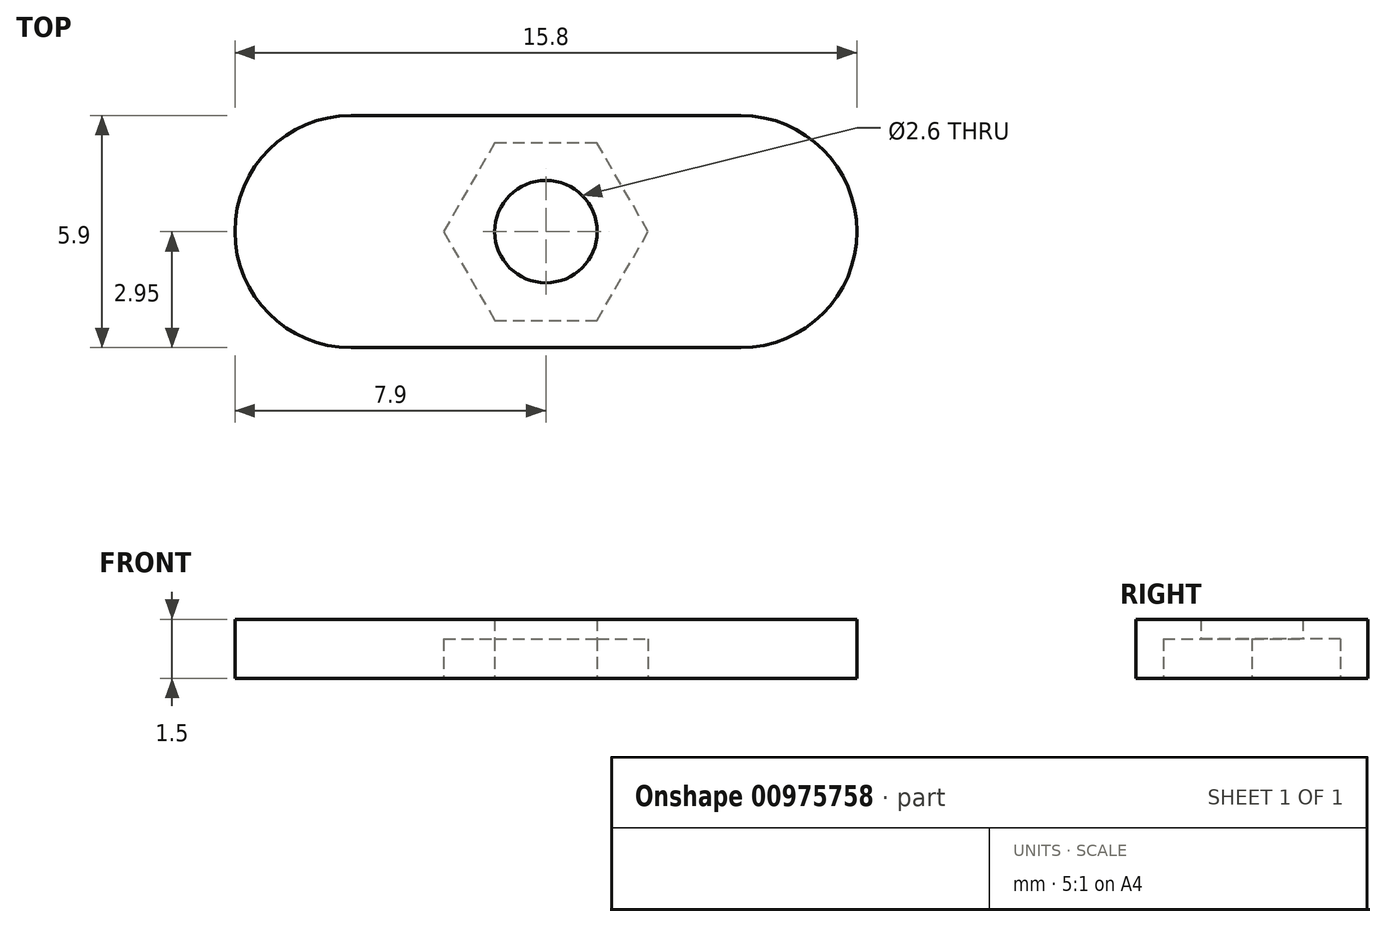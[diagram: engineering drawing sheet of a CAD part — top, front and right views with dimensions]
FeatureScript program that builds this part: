
annotation { "Feature Type Name" : "Feature", "Feature Type Description" : "" }
export const myFeature = defineFeature(function(context is Context, id is Id, definition is map)
    precondition{}
    {
        {
            var Q0;
            Q0=qCreatedBy(makeId("Top.planeOp"),FACE);
            var sketch = newSketch(context, id + "F0", { "sketchPlane" : qUnion([Q0])});
            skLineSegment(sketch, "E0", {"start": v(0, 0) * mm, "end": v(4.95, 0) * mm});
            skLineSegment(sketch, "E1", {"start": v(0, 0) * mm, "end": v(-4.95, 0) * mm});
            skCircle(sketch, "E2", {"center": v(-4.95, 0) * mm, "radius": 2.95 * mm});
            skCircle(sketch, "E3", {"center": v(4.95, 0) * mm, "radius": 2.95 * mm});
            skLineSegment(sketch, "E4", {"start": v(4.95, 0) * mm, "end": v(4.95, 2.95) * mm});
            skLineSegment(sketch, "E5", {"start": v(4.95, 2.95) * mm, "end": v(-4.95, 2.95) * mm});
            skLineSegment(sketch, "E6", {"start": v(-4.95, -2.95) * mm, "end": v(4.95, -2.95) * mm});
            skSolve(sketch);
        }
        {
            var Q0;
            Q0 = qSketchRegion(id + "F0", true);
            extrude(context, id + "F1", {"entities" : qUnion([Q0]), "depth" : 1.5 * mm, "offsetDistance" : 25 * mm});
        }
        {
            var Q0;
            Q0=makeQuery(id+"F1.opExtrude","CAP_FACE",FACE,{"disambiguationData":[OSD([sQuery(id+"F0.wireOp",EDGE,"E2"),sQuery(id+"F0.wireOp",EDGE,"E3"),sQuery(id+"F0.wireOp",EDGE,"E5"),sQuery(id+"F0.wireOp",EDGE,"E6")])],"isStart":true});
            var sketch = newSketch(context, id + "F2", { "sketchPlane" : qUnion([Q0])});
            skCircle(sketch, "E7", {"center": v(0, 0) * mm, "radius": 2.6 * mm});
            skCircle(sketch, "E8.cCircle", {"center": v(0, 0) * mm, "radius": 2.6 * mm, "construction": true});
            skLineSegment(sketch, "E8.0", {"start": v(-2.6, 0) * mm, "end": v(-1.3, 2.25) * mm});
            skLineSegment(sketch, "E8.1", {"start": v(-1.3, 2.25) * mm, "end": v(1.3, 2.25) * mm});
            skLineSegment(sketch, "E8.2", {"start": v(1.3, 2.25) * mm, "end": v(2.6, 0) * mm});
            skLineSegment(sketch, "E8.3", {"start": v(2.6, 0) * mm, "end": v(1.3, -2.25) * mm});
            skLineSegment(sketch, "E8.4", {"start": v(1.3, -2.25) * mm, "end": v(-1.3, -2.25) * mm});
            skLineSegment(sketch, "E8.5", {"start": v(-1.3, -2.25) * mm, "end": v(-2.6, 0) * mm});
            skSolve(sketch);
        }
        {
            var Q0;
            Q0=makeQuery(id+"F2.imprint","IMPRINT",FACE,{"disambiguationData":[TD([[makeQuery(id+"F2.imprint","IMPRINT",EDGE,{"derivedFrom":sQuery(id+"F2.wireOp",EDGE,"E8.0")}),-1.0]])]});
            extrude(context, id + "F3", {"entities" : qUnion([Q0]), "operationType" : NewBodyOperationType.REMOVE, "oppositeDirection" : true, "depth" : 1 * mm, "offsetDistance" : 25 * mm});
        }
        {
            var Q0;
            Q0=makeQuery(id+"F3.boolean.opBoolean","COPY",FACE,{"derivedFrom":makeQuery(id+"F3.opExtrude","CAP_FACE",FACE,{"disambiguationData":[OSD([sQuery(id+"F2.wireOp",EDGE,"E8.0"),sQuery(id+"F2.wireOp",EDGE,"E8.1"),sQuery(id+"F2.wireOp",EDGE,"E8.2"),sQuery(id+"F2.wireOp",EDGE,"E8.3"),sQuery(id+"F2.wireOp",EDGE,"E8.4"),sQuery(id+"F2.wireOp",EDGE,"E8.5")])],"isStart":false})});
            var sketch = newSketch(context, id + "F4", { "sketchPlane" : qUnion([Q0])});
            skCircle(sketch, "E9", {"center": v(0, 0) * mm, "radius": 1.3 * mm});
            skSolve(sketch);
        }
        {
            var Q0;
            Q0 = qSketchRegion(id + "F4", true);
            extrude(context, id + "F5", {"entities" : qUnion([Q0]), "operationType" : NewBodyOperationType.REMOVE, "oppositeDirection" : true, "depth" : 25 * mm, "offsetDistance" : 25 * mm});
        }
    });
